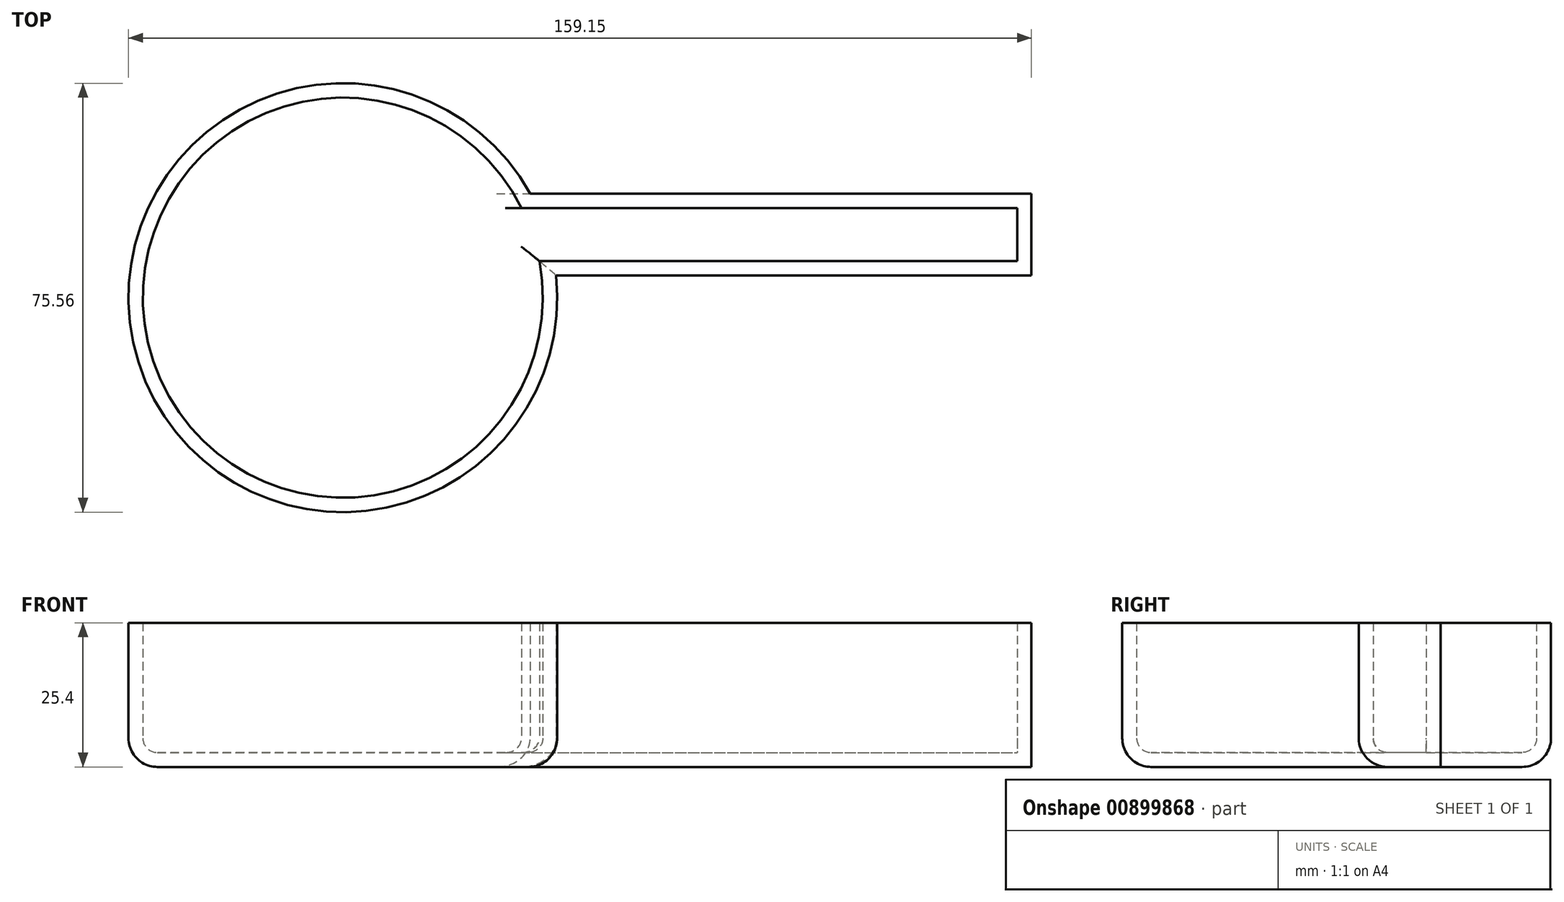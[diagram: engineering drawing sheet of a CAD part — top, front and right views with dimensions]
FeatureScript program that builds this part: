
annotation { "Feature Type Name" : "Feature", "Feature Type Description" : "" }
export const myFeature = defineFeature(function(context is Context, id is Id, definition is map)
    precondition{}
    {
        {
            var Q0;
            Q0=qCreatedBy(makeId("Top.planeOp"),FACE);
            var sketch = newSketch(context, id + "F0", { "sketchPlane" : qUnion([Q0])});
            skArc(sketch, "E0", {"start": v(33.04, 18.33) * mm, "mid": v(-36.04, -11.35) * mm, "end": v(37.58, 3.9) * mm});
            skLineSegment(sketch, "E1.bottom", {"start": v(33.04, 18.33) * mm, "end": v(121.37, 18.33) * mm});
            skLineSegment(sketch, "E1.top", {"start": v(37.58, 3.9) * mm, "end": v(121.37, 3.9) * mm});
            skLineSegment(sketch, "E1.right", {"start": v(121.37, 18.33) * mm, "end": v(121.37, 3.9) * mm});
            skSolve(sketch);
        }
        {
            var Q0;
            Q0 = qSketchRegion(id + "F0", true);
            extrude(context, id + "F1", {"entities" : qUnion([Q0]), "depth" : 25.4 * mm, "offsetDistance" : 25.4 * mm});
        }
        {
            var Q0;
            Q0=makeQuery(id+"F1.opExtrude","CAP_EDGE",EDGE,{"disambiguationData":[OSD([sQuery(id+"F0.wireOp",EDGE,"E0")])],"isStart":true});
            fillet(context, id + "F2", {"entities" : qUnion([Q0]), "radius" : 5.08 * mm, "tangentPropagation" : true, "allowEdgeOverflow" : false});
        }
        {
            var Q0;
            Q0=makeQuery(id+"F1.opExtrude","CAP_EDGE",EDGE,{"disambiguationData":[OSD([sQuery(id+"F0.wireOp",EDGE,"E1.top")])],"isStart":true});
            fillet(context, id + "F3", {"entities" : qUnion([Q0]), "radius" : 5.08 * mm, "tangentPropagation" : true, "allowEdgeOverflow" : false});
        }
        {
            var Q0;
            Q0=makeQuery(id+"F1.opExtrude","CAP_FACE",FACE,{"disambiguationData":[OSD([sQuery(id+"F0.wireOp",EDGE,"E0"),sQuery(id+"F0.wireOp",EDGE,"E1.bottom"),sQuery(id+"F0.wireOp",EDGE,"E1.top"),sQuery(id+"F0.wireOp",EDGE,"E1.right")])],"isStart":false});
            shell(context, id + "F4", {"entities" : qUnion([Q0]), "thickness" : 2.54 * mm});
        }
    });
